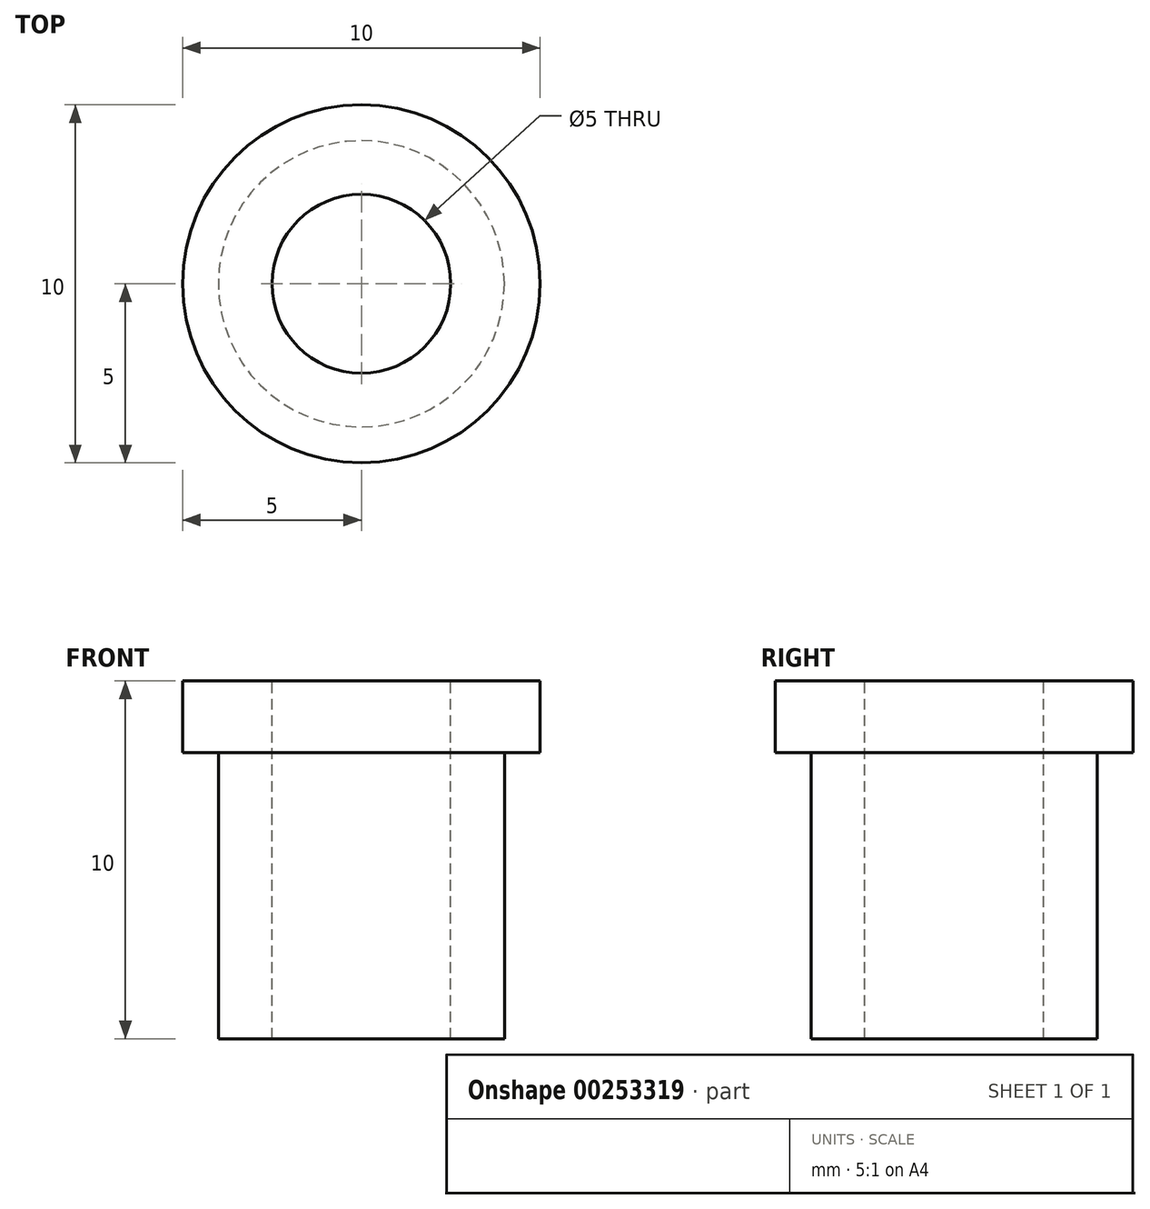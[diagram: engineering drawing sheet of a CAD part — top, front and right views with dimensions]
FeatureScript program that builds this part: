
annotation { "Feature Type Name" : "Feature", "Feature Type Description" : "" }
export const myFeature = defineFeature(function(context is Context, id is Id, definition is map)
    precondition{}
    {
        {
            var Q0;
            Q0=qCreatedBy(makeId("Front.planeOp"),FACE);
            var sketch = newSketch(context, id + "F0", { "sketchPlane" : qUnion([Q0])});
            skLineSegment(sketch, "E0", {"start": v(0, 10) * mm, "end": v(-5, 10) * mm, "construction": true});
            skLineSegment(sketch, "E1", {"start": v(-5, 10) * mm, "end": v(-5, 8) * mm, "construction": true});
            skLineSegment(sketch, "E2", {"start": v(-5, 8) * mm, "end": v(-4, 8) * mm, "construction": true});
            skLineSegment(sketch, "E3", {"start": v(-4, 8) * mm, "end": v(-4, 0) * mm, "construction": true});
            skLineSegment(sketch, "E4", {"start": v(-4, 0) * mm, "end": v(0, 0) * mm, "construction": true});
            skLineSegment(sketch, "E5.MirrorCS", {"start": v(0, 10) * mm, "end": v(5, 10) * mm});
            skLineSegment(sketch, "E6.MirrorCS", {"start": v(5, 10) * mm, "end": v(5, 8) * mm});
            skLineSegment(sketch, "E7.MirrorCS", {"start": v(5, 8) * mm, "end": v(4, 8) * mm});
            skLineSegment(sketch, "E8.MirrorCS", {"start": v(4, 8) * mm, "end": v(4, 0) * mm});
            skLineSegment(sketch, "E9.MirrorCS", {"start": v(4, 0) * mm, "end": v(0, 0) * mm});
            skLineSegment(sketch, "E10", {"start": v(0, 17.23) * mm, "end": v(0, -2.24) * mm, "construction": true});
            skLineSegment(sketch, "E11", {"start": v(0, 10) * mm, "end": v(0, 0) * mm});
            skSolve(sketch);
        }
        {
            var Q0;
            Q0 = qSketchRegion(id + "F0", true);
            var Q1;
            Q1=sQuery(id+"F0.wireOp",EDGE,"E11");
            revolve(context, id + "F1", {"entities" : qUnion([Q0]), "axis" : qUnion([Q1]), "revolveType" : RevolveType.FULL});
        }
        {
            var Q0;
            Q0=makeQuery(id+"F1.opRevolve","SWEPT_FACE",FACE,{"disambiguationData":[OSD([sQuery(id+"F0.wireOp",EDGE,"E5.MirrorCS")])]});
            var sketch = newSketch(context, id + "F2", { "sketchPlane" : qUnion([Q0])});
            skCircle(sketch, "E12", {"center": v(0, 0) * mm, "radius": 2.5 * mm});
            skSolve(sketch);
        }
        {
            var Q0;
            Q0 = qSketchRegion(id + "F2", true);
            extrude(context, id + "F3", {"entities" : qUnion([Q0]), "operationType" : NewBodyOperationType.REMOVE, "oppositeDirection" : true, "depth" : 25 * mm});
        }
    });
